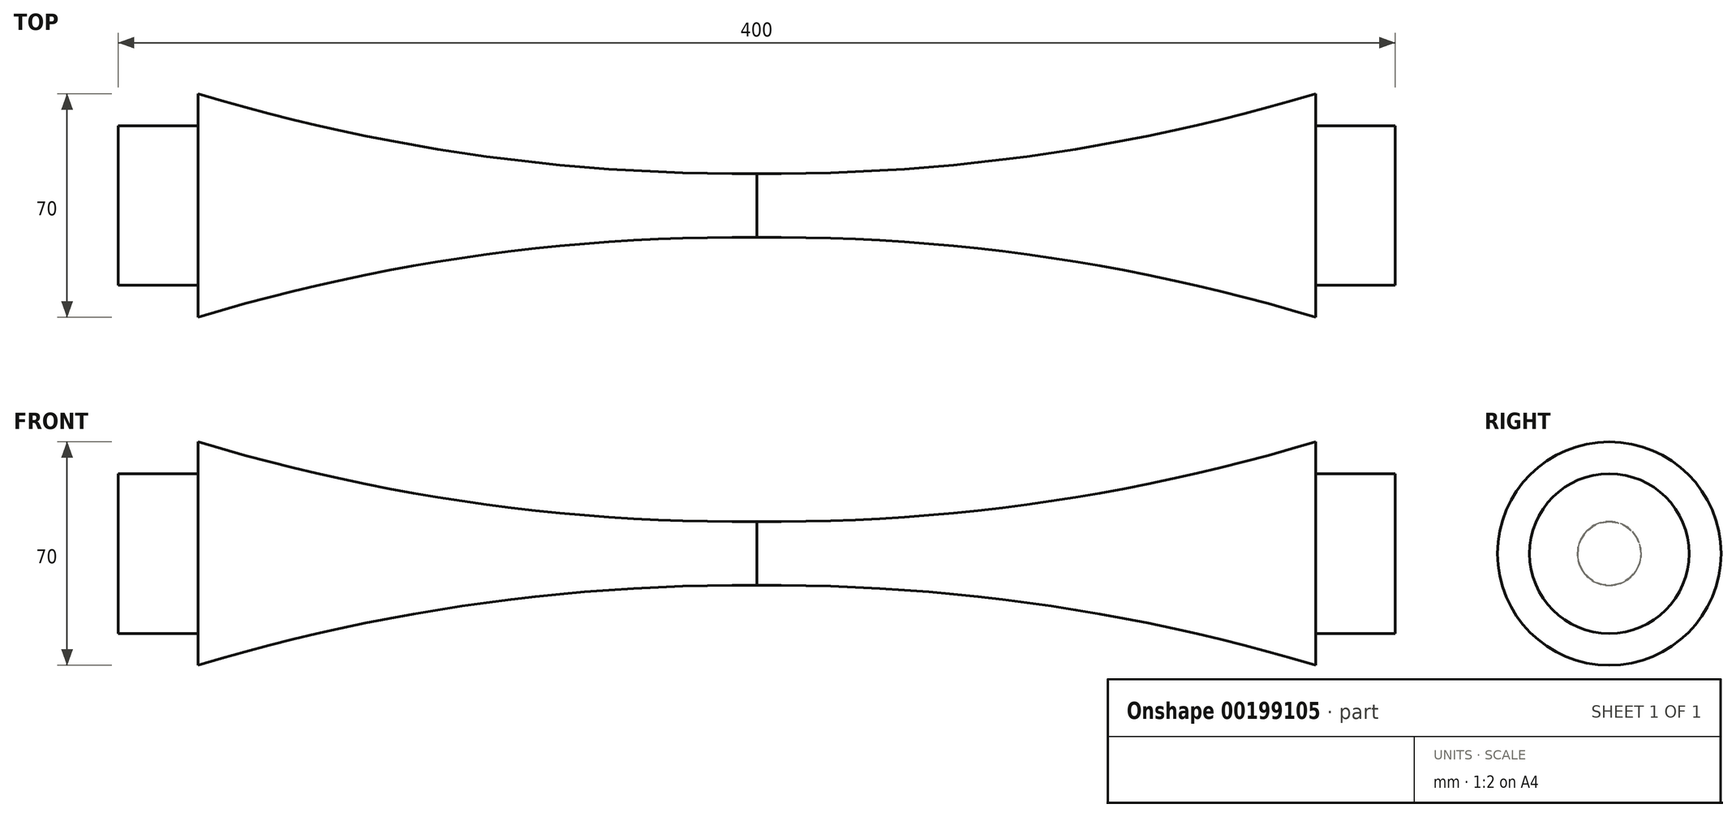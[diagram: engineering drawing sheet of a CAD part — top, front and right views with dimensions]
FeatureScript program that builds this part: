
annotation { "Feature Type Name" : "Feature", "Feature Type Description" : "" }
export const myFeature = defineFeature(function(context is Context, id is Id, definition is map)
    precondition{}
    {
        {
            var Q0;
            Q0=qCreatedBy(makeId("Front.planeOp"),FACE);
            var sketch = newSketch(context, id + "F0", { "sketchPlane" : qUnion([Q0])});
            skLineSegment(sketch, "E0", {"start": v(-65.56, 15.2) * mm, "end": v(-65.56, -9.8) * mm});
            skLineSegment(sketch, "E1", {"start": v(-65.56, -9.8) * mm, "end": v(134.44, -9.8) * mm});
            skLineSegment(sketch, "E2", {"start": v(134.44, -9.8) * mm, "end": v(134.44, 0.2) * mm});
            skLineSegment(sketch, "E3", {"start": v(-65.56, 15.2) * mm, "end": v(-40.56, 15.2) * mm});
            skLineSegment(sketch, "E4", {"start": v(-40.56, 15.2) * mm, "end": v(-40.56, 25.2) * mm});
            skArc(sketch, "E5", {"start": v(-40.56, 25.2) * mm, "mid": v(46, 6.1) * mm, "end": v(134.44, 0.2) * mm});
            skSolve(sketch);
        }
        {
            var Q0;
            Q0=makeQuery(id+"F0.imprint","IMPRINT",FACE,{"disambiguationData":[TD([[makeQuery(id+"F0.imprint","IMPRINT",EDGE,{"derivedFrom":sQuery(id+"F0.wireOp",EDGE,"E0")}),1.0]])]});
            var Q1;
            Q1=sQuery(id+"F0.wireOp",EDGE,"E1");
            revolve(context, id + "F1", {"entities" : qUnion([Q0]), "axis" : qUnion([Q1]), "revolveType" : RevolveType.FULL});
        }
        {
            var Q0;
            Q0=makeQuery(id+"F1.opRevolve","SWEPT_BODY",BODY,{"disambiguationData":[OSD([sQuery(id+"F0.wireOp",EDGE,"E0"),sQuery(id+"F0.wireOp",EDGE,"E1"),sQuery(id+"F0.wireOp",EDGE,"E2"),sQuery(id+"F0.wireOp",EDGE,"E3"),sQuery(id+"F0.wireOp",EDGE,"E4"),sQuery(id+"F0.wireOp",EDGE,"Z9wayshn-SFpM-fpmJ-O2Ia-lMpgPGRvs6PJ")])]});
            var Q1;
            Q1=makeQuery(id+"F1.opRevolve","SWEPT_FACE",FACE,{"disambiguationData":[OSD([sQuery(id+"F0.wireOp",EDGE,"E2")])]});
            mirror(context, id + "F2", {"operationType" : NewBodyOperationType.ADD, "entities" : qUnion([Q0]), "mirrorPlane" : qUnion([Q1])});
        }
    });
